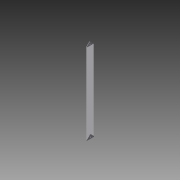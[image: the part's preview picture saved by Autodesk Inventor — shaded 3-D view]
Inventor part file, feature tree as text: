
AUTODESK INVENTOR PART (.ipt)
format: ipt  version: 2015 SP1 (Build 190203100, 203)  size: 99,328 bytes
history: native  units: in
note: dims shown in document units (in); Inventor stores cm internally (conversion verified against a paired STEP export)
features: extrude x3, sketch x3, projected_geometry x2
ambient origin geometry x8: Origin, YZ Plane, XZ Plane, XY Plane, X Axis, Y Axis, Z Axis, Center Point
bodies: Solid1 (feature_tree)
feature tree (8):
  extrude  "Extrusion1"  Depth=31.0in
  extrude  "Extrusion4"  TaperAngle=90.0deg  [1 undecoded]
  extrude  "Extrusion6"  TaperAngle=90.0deg  [1 undecoded]
  sketch  "Sketch1"  dims[d0=20.75in d1=31.0in]
  sketch  "Sketch6"  dims[d2=2.0in d3=90.0deg]
  projected_geometry  "Projected Loop5"
  sketch  "Sketch8"  dims[d4=2.0in d5=90.0deg d6=0.125in d7=0.0in d33=135.0deg d34=0.125in d35=0.0in d38=0.125in d39=0.0in]
  projected_geometry  "Projected Loop7"
note: 2 required parameter values undecoded (feature->parameter linkage not recoverable at this tier; creation-order binding heuristic only, values carry confidence <= 0.55)
